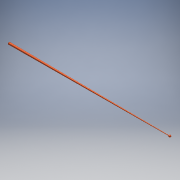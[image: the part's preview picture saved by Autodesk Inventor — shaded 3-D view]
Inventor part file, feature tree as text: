
AUTODESK INVENTOR PART (.ipt)
format: ipt  version: 2016 (Build 200138000, 138)  size: 106,496 bytes
history: native  units: mm
features: sketch x3, plane x1, loft x1, revolve x1
ambient origin geometry x8: Origin, YZ Plane, XZ Plane, XY Plane, X Axis, Y Axis, Z Axis, Center Point
bodies: Solid1 (feature_tree)
feature tree (6):
  sketch  "Sketch1"  dims[d0=20.0mm d1=1500.0mm]
  plane  "Work Plane1"
  loft  "Loft1"
  revolve  "Revolution1"  Angle=90.0deg
  sketch  "Sketch2"  dims[d2=5.0mm d3=0.0mm d4=90.0deg]
  sketch  "Sketch3"  dims[d5=0.0mm d6=90.0deg d7=20.0mm d8=0.0mm d9=90.0deg]
